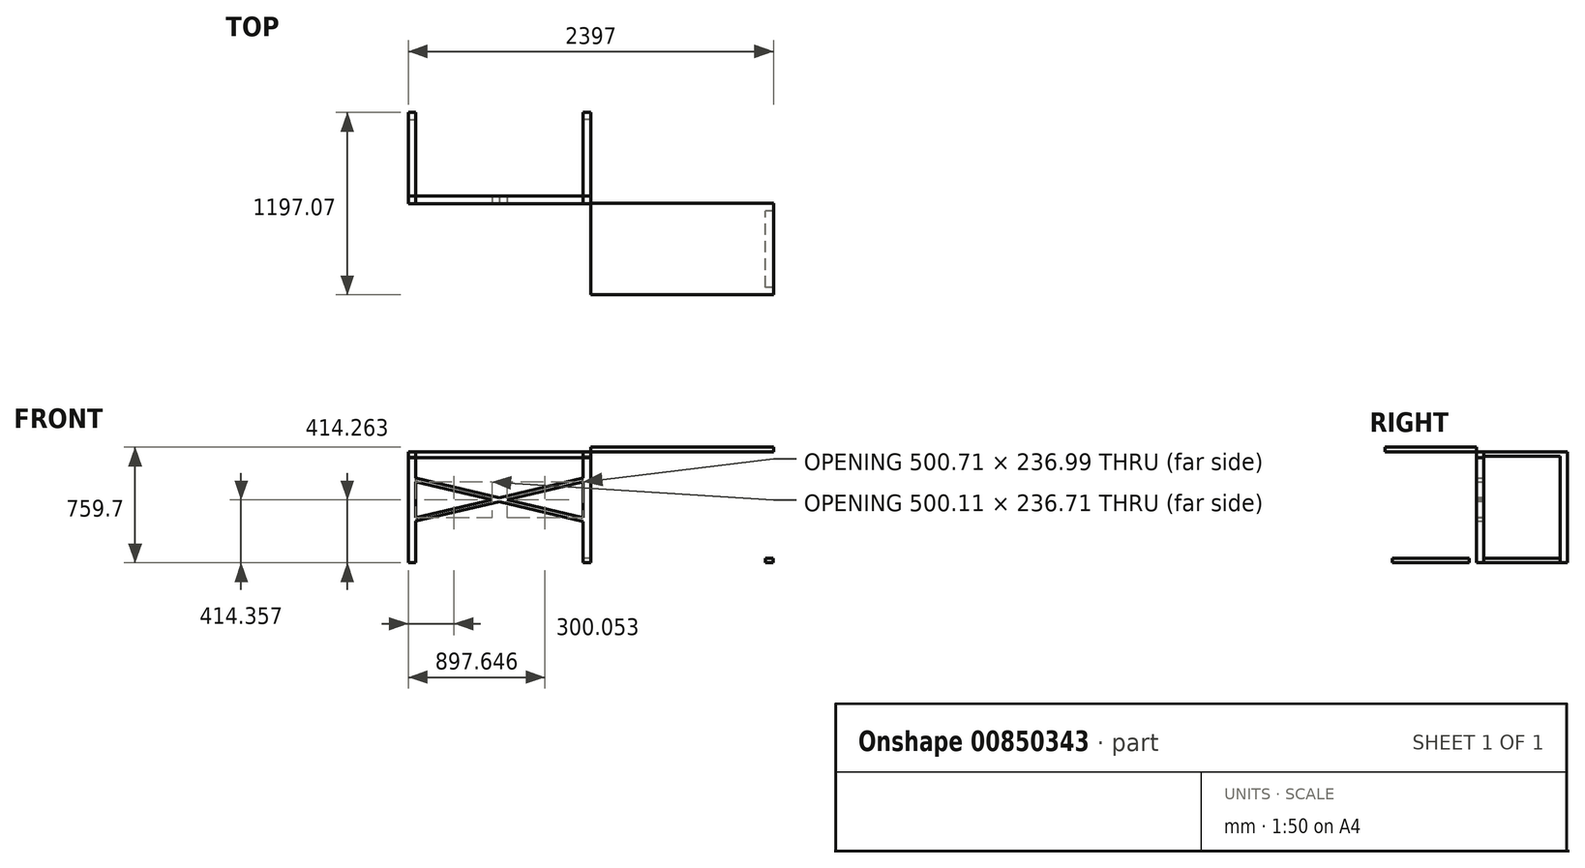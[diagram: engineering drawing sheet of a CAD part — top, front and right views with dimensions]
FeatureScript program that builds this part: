
annotation { "Feature Type Name" : "Feature", "Feature Type Description" : "" }
export const myFeature = defineFeature(function(context is Context, id is Id, definition is map)
    precondition{}
    {
        {
            var Q0;
            Q0=qCreatedBy(makeId("Top.planeOp"),FACE);
            var sketch = newSketch(context, id + "F0", { "sketchPlane" : qUnion([Q0])});
            skLineSegment(sketch, "E0.bottom", {"start": v(600, -300) * mm, "end": v(-600, -300) * mm});
            skLineSegment(sketch, "E0.top", {"start": v(600, 300) * mm, "end": v(-600, 300) * mm});
            skLineSegment(sketch, "E0.left", {"start": v(600, -300) * mm, "end": v(600, 300) * mm});
            skLineSegment(sketch, "E0.right", {"start": v(-600, -300) * mm, "end": v(-600, 300) * mm});
            skPoint(sketch, "E0.middle", {"position": v(0, 0) * mm});
            skSolve(sketch);
        }
        {
            var Q0;
            Q0=qSketchRegion(id+"F0",true);
            extrude(context, id + "F1", {"entities" : qUnion([Q0]), "depth" : 30 * mm, "offsetDistance" : 25 * mm});
        }
        {
            var Q0;
            Q0=qCreatedBy(makeId("Right.planeOp"),FACE);
            var sketch = newSketch(context, id + "F2", { "sketchPlane" : qUnion([Q0])});
            skLineSegment(sketch, "E1.bottom", {"start": v(-299.02, 0) * mm, "end": v(299.02, 0) * mm});
            skLineSegment(sketch, "E1.top", {"start": v(-299.02, -29.7) * mm, "end": v(299.02, -29.7) * mm});
            skLineSegment(sketch, "E1.left", {"start": v(-299.02, 0) * mm, "end": v(-299.02, -29.7) * mm});
            skLineSegment(sketch, "E1.right", {"start": v(299.02, 0) * mm, "end": v(299.02, -29.7) * mm});
            skSolve(sketch);
        }
        {
            var Q0;
            Q0=qSketchRegion(id+"F2",true);
            extrude(context, id + "F3", {"entities" : qUnion([Q0]), "depth" : 50 * mm, "offsetDistance" : 25 * mm});
        }
        {
            var Q0;
            Q0=makeQuery(id+"F3.opExtrude","SWEPT_BODY",BODY,{"disambiguationData":[OSD([sQuery(id+"F2.wireOp",EDGE,"E1.bottom"),sQuery(id+"F2.wireOp",EDGE,"E1.top"),sQuery(id+"F2.wireOp",EDGE,"E1.left"),sQuery(id+"F2.wireOp",EDGE,"E1.right")])]});
            transform(context, id + "F4", {"entities" : qUnion([Q0]), "transformType" : TransformType.TRANSLATION_3D, "dx" : 549 * mm, "dy" : 0 * mm, "dz" : 0 * mm, "makeCopy" : false});
        }
        {
            var Q0;
            Q0=makeQuery(id+"F3.opExtrude","SWEPT_BODY",BODY,{"disambiguationData":[OSD([sQuery(id+"F2.wireOp",EDGE,"E1.bottom"),sQuery(id+"F2.wireOp",EDGE,"E1.top"),sQuery(id+"F2.wireOp",EDGE,"E1.left"),sQuery(id+"F2.wireOp",EDGE,"E1.right")])]});
            var Q1;
            Q1=qCreatedBy(makeId("Right.planeOp"),FACE);
            mirror(context, id + "F5", {"entities" : qUnion([Q0]), "mirrorPlane" : qUnion([Q1])});
        }
        {
            var Q0;
            Q0=makeQuery(id+"F5.opPattern","COPY",FACE,{"derivedFrom":makeQuery(id+"F3.opExtrude","SWEPT_FACE",FACE,{"disambiguationData":[OSD([sQuery(id+"F2.wireOp",EDGE,"E1.top")])]}),"instanceName":"1"});
            var sketch = newSketch(context, id + "F6", { "sketchPlane" : qUnion([Q0])});
            skLineSegment(sketch, "E2.bottom", {"start": v(-599, -299.02) * mm, "end": v(-549, -299.02) * mm});
            skLineSegment(sketch, "E2.top", {"start": v(-599, -251.22) * mm, "end": v(-549, -251.22) * mm});
            skLineSegment(sketch, "E2.left", {"start": v(-599, -299.02) * mm, "end": v(-599, -251.22) * mm});
            skLineSegment(sketch, "E2.right", {"start": v(-549, -299.02) * mm, "end": v(-549, -251.22) * mm});
            skSolve(sketch);
        }
        {
            var Q0;
            Q0=qSketchRegion(id+"F6",true);
            extrude(context, id + "F7", {"entities" : qUnion([Q0]), "depth" : 700 * mm, "offsetDistance" : 25 * mm});
        }
        {
            var Q0;
            Q0=makeQuery(id+"F7.opExtrude","SWEPT_BODY",BODY,{"disambiguationData":[OSD([sQuery(id+"F6.wireOp",EDGE,"E2.bottom"),sQuery(id+"F6.wireOp",EDGE,"E2.top"),sQuery(id+"F6.wireOp",EDGE,"E2.left"),sQuery(id+"F6.wireOp",EDGE,"E2.right")])]});
            var Q1;
            Q1=qCreatedBy(makeId("Right.planeOp"),FACE);
            mirror(context, id + "F8", {"entities" : qUnion([Q0]), "mirrorPlane" : qUnion([Q1])});
        }
        {
            var Q0;
            Q0=makeQuery(id+"F7.opExtrude","SWEPT_BODY",BODY,{"disambiguationData":[OSD([sQuery(id+"F6.wireOp",EDGE,"E2.bottom"),sQuery(id+"F6.wireOp",EDGE,"E2.top"),sQuery(id+"F6.wireOp",EDGE,"E2.left"),sQuery(id+"F6.wireOp",EDGE,"E2.right")])]});
            var Q1;
            Q1=qCreatedBy(makeId("Front.planeOp"),FACE);
            mirror(context, id + "F9", {"operationType" : NewBodyOperationType.ADD, "entities" : qUnion([Q0]), "mirrorPlane" : qUnion([Q1])});
        }
        {
            var Q0;
            Q0=makeQuery(id+"F8.opPattern","COPY",BODY,{"derivedFrom":makeQuery(id+"F7.opExtrude","SWEPT_BODY",BODY,{"disambiguationData":[OSD([sQuery(id+"F6.wireOp",EDGE,"E2.bottom"),sQuery(id+"F6.wireOp",EDGE,"E2.top"),sQuery(id+"F6.wireOp",EDGE,"E2.left"),sQuery(id+"F6.wireOp",EDGE,"E2.right")])]}),"instanceName":"1"});
            var Q1;
            Q1=qCreatedBy(makeId("Front.planeOp"),FACE);
            mirror(context, id + "F10", {"operationType" : NewBodyOperationType.ADD, "entities" : qUnion([Q0]), "mirrorPlane" : qUnion([Q1])});
        }
        {
            var Q0;
            Q0=qCreatedBy(makeId("Top.planeOp"),FACE);
            var sketch = newSketch(context, id + "F11", { "sketchPlane" : qUnion([Q0])});
            skLineSegment(sketch, "E3.bottom", {"start": v(-598.92, -299.03) * mm, "end": v(598.98, -299.03) * mm});
            skLineSegment(sketch, "E3.top", {"start": v(-598.92, -251.27) * mm, "end": v(598.98, -251.27) * mm});
            skLineSegment(sketch, "E3.left", {"start": v(-598.92, -299.03) * mm, "end": v(-598.92, -251.27) * mm});
            skLineSegment(sketch, "E3.right", {"start": v(598.98, -299.03) * mm, "end": v(598.98, -251.27) * mm});
            skSolve(sketch);
        }
        {
            var Q0;
            Q0=qSketchRegion(id+"F11",true);
            extrude(context, id + "F12", {"entities" : qUnion([Q0]), "oppositeDirection" : true, "depth" : 40 * mm, "offsetDistance" : 25 * mm});
        }
        {
            var Q0;
            Q0=makeQuery(id+"F9.opPattern","COPY",FACE,{"derivedFrom":makeQuery(id+"F7.opExtrude","SWEPT_FACE",FACE,{"disambiguationData":[OSD([sQuery(id+"F6.wireOp",EDGE,"E2.top")])]}),"instanceName":"1"});
            var sketch = newSketch(context, id + "F13", { "sketchPlane" : qUnion([Q0])});
            skLineSegment(sketch, "E4.bottom", {"start": v(599, -729.7) * mm, "end": v(549, -729.7) * mm});
            skLineSegment(sketch, "E4.top", {"start": v(599, -699.7) * mm, "end": v(549, -699.7) * mm});
            skLineSegment(sketch, "E4.left", {"start": v(599, -729.7) * mm, "end": v(599, -699.7) * mm});
            skLineSegment(sketch, "E4.right", {"start": v(549, -729.7) * mm, "end": v(549, -699.7) * mm});
            skLineSegment(sketch, "E5.MirrorCS", {"start": v(-599, -729.7) * mm, "end": v(-599, -699.7) * mm});
            skLineSegment(sketch, "E6.MirrorCS", {"start": v(-599, -729.7) * mm, "end": v(-549, -729.7) * mm});
            skLineSegment(sketch, "E7.MirrorCS", {"start": v(-599, -699.7) * mm, "end": v(-549, -699.7) * mm});
            skLineSegment(sketch, "E8.MirrorCS", {"start": v(-549, -729.7) * mm, "end": v(-549, -699.7) * mm});
            skSolve(sketch);
        }
        {
            var Q0;
            Q0=qSketchRegion(id+"F13",true);
            extrude(context, id + "F14", {"entities" : qUnion([Q0]), "depth" : 502.5 * mm, "offsetDistance" : 25 * mm});
        }
        {
            var Q0;
            {var subQ0=makeQuery(id+"F7.opExtrude","SWEPT_FACE",FACE,{"disambiguationData":[OSD([sQuery(id+"F6.wireOp",EDGE,"E2.right")])]});Q0=makeQuery(id+"F9.boolean.opBoolean","MERGE",FACE,{"derivedFrom":[makeQuery(id+"F5.opPattern","COPY",FACE,{"derivedFrom":makeQuery(id+"F3.opExtrude","CAP_FACE",FACE,{"disambiguationData":[OSD([sQuery(id+"F2.wireOp",EDGE,"E1.bottom"),sQuery(id+"F2.wireOp",EDGE,"E1.top"),sQuery(id+"F2.wireOp",EDGE,"E1.left"),sQuery(id+"F2.wireOp",EDGE,"E1.right")])],"isStart":true}),"instanceName":"1"}),subQ0,makeQuery(id+"F9.opPattern","COPY",FACE,{"derivedFrom":subQ0,"instanceName":"1"})]});}
            var sketch = newSketch(context, id + "F15", { "sketchPlane" : qUnion([Q0])});
            skLineSegment(sketch, "E9.bottom", {"start": v(-299.02, -174.08) * mm, "end": v(-251.22, -174.08) * mm});
            skLineSegment(sketch, "E9.top", {"start": v(-299.02, -197.08) * mm, "end": v(-251.22, -197.08) * mm});
            skLineSegment(sketch, "E9.left", {"start": v(-299.02, -174.08) * mm, "end": v(-299.02, -197.08) * mm});
            skLineSegment(sketch, "E9.right", {"start": v(-251.22, -174.08) * mm, "end": v(-251.22, -197.08) * mm});
            skSolve(sketch);
        }
        {
            var Q0;
            {var subQ0=makeQuery(id+"F8.opPattern","COPY",FACE,{"derivedFrom":makeQuery(id+"F7.opExtrude","SWEPT_FACE",FACE,{"disambiguationData":[OSD([sQuery(id+"F6.wireOp",EDGE,"E2.right")])]}),"instanceName":"1"});Q0=makeQuery(id+"F10.boolean.opBoolean","MERGE",FACE,{"derivedFrom":[makeQuery(id+"F3.opExtrude","CAP_FACE",FACE,{"disambiguationData":[OSD([sQuery(id+"F2.wireOp",EDGE,"E1.bottom"),sQuery(id+"F2.wireOp",EDGE,"E1.top"),sQuery(id+"F2.wireOp",EDGE,"E1.left"),sQuery(id+"F2.wireOp",EDGE,"E1.right")])],"isStart":true}),subQ0,makeQuery(id+"F10.opPattern","COPY",FACE,{"derivedFrom":subQ0,"instanceName":"1"})]});}
            var sketch = newSketch(context, id + "F16", { "sketchPlane" : qUnion([Q0])});
            skLineSegment(sketch, "E10.bottom", {"start": v(251.22, -433.84) * mm, "end": v(299.02, -433.84) * mm});
            skLineSegment(sketch, "E10.top", {"start": v(251.22, -456.84) * mm, "end": v(299.02, -456.84) * mm});
            skLineSegment(sketch, "E10.left", {"start": v(251.22, -433.84) * mm, "end": v(251.22, -456.84) * mm});
            skLineSegment(sketch, "E10.right", {"start": v(299.02, -433.84) * mm, "end": v(299.02, -456.84) * mm});
            skSolve(sketch);
        }
        {
            var Q2;
            Q2=makeQuery(id+"F15.imprint","IMPRINT",FACE,{"disambiguationData":[TD([[makeQuery(id+"F15.imprint","IMPRINT",EDGE,{"derivedFrom":sQuery(id+"F15.wireOp",EDGE,"E9.bottom")}),-1.0]])]});
            var Q3;
            Q3=makeQuery(id+"F16.imprint","IMPRINT",FACE,{"disambiguationData":[TD([[makeQuery(id+"F16.imprint","IMPRINT",EDGE,{"derivedFrom":sQuery(id+"F16.wireOp",EDGE,"E10.bottom")}),-1.0]])]});
            loft(context, id + "F17", {"operationType" : NewBodyOperationType.ADD, "sheetProfilesArray" : [{ "sheetProfileEntities" : qUnion([Q2]) }, { "sheetProfileEntities" : qUnion([Q3]) }]});
        }
        {
            var Q0;
            {var subQ0=sQuery(id+"F6.wireOp",EDGE,"E2.top");var subQ9=sQuery(id+"F6.wireOp",EDGE,"E2.right");var subQ10=sQuery(id+"F2.wireOp",EDGE,"E1.top");var subQ12=sQuery(id+"F6.wireOp",EDGE,"E2.bottom");var subQ17=sQuery(id+"F2.wireOp",EDGE,"E1.left");var subQ22=makeQuery(id+"F8.opPattern","COPY",FACE,{"derivedFrom":makeQuery(id+"F7.opExtrude","CAP_FACE",FACE,{"disambiguationData":[OSD([subQ12,subQ0,sQuery(id+"F6.wireOp",EDGE,"E2.left"),subQ9])],"isStart":false}),"instanceName":"1"});var subQ26=makeQuery(id+"F8.opPattern","COPY",FACE,{"derivedFrom":makeQuery(id+"F7.opExtrude","SWEPT_FACE",FACE,{"disambiguationData":[OSD([subQ9])]}),"instanceName":"1"});var subQ27=sQuery(id+"F2.wireOp",EDGE,"E1.right");var subQ28=sQuery(id+"F2.wireOp",EDGE,"E1.bottom");var subQ29=makeQuery(id+"F10.boolean.opBoolean","MERGE",FACE,{"derivedFrom":[makeQuery(id+"F3.opExtrude","CAP_FACE",FACE,{"disambiguationData":[OSD([subQ28,subQ10,subQ17,subQ27])],"isStart":true}),subQ26,makeQuery(id+"F10.opPattern","COPY",FACE,{"derivedFrom":subQ26,"instanceName":"1"})]});Q0=makeQuery(id+"FEgc4e0kRUvku2v_5.opBoolean","MERGE",FACE,{"derivedFrom":[makeQuery(id+"F14.opExtrude","SWEPT_FACE",FACE,{"disambiguationData":[OSD([sQuery(id+"F13.wireOp",EDGE,"E8.MirrorCS")])]}),makeQuery(id+"F17.boolean.opBoolean","SPLIT",FACE,{"disambiguationData":[TD([makeQuery(id+"F3.opExtrude","SWEPT_FACE",FACE,{"disambiguationData":[OSD([subQ28])]})])],"derivedFrom":subQ29}),makeQuery(id+"F17.boolean.opBoolean","SPLIT",FACE,{"disambiguationData":[TD([makeQuery(id+"F10.opPattern","COPY",FACE,{"derivedFrom":subQ22,"instanceName":"1"})])],"derivedFrom":subQ29})]});}
            var sketch = newSketch(context, id + "F18", { "sketchPlane" : qUnion([Q0])});
            skLineSegment(sketch, "E11.bottom", {"start": v(299.02, -173.85) * mm, "end": v(251.22, -173.85) * mm});
            skLineSegment(sketch, "E11.top", {"start": v(299.02, -196.85) * mm, "end": v(251.22, -196.85) * mm});
            skLineSegment(sketch, "E11.left", {"start": v(299.02, -173.85) * mm, "end": v(299.02, -196.85) * mm});
            skLineSegment(sketch, "E11.right", {"start": v(251.22, -173.85) * mm, "end": v(251.22, -196.85) * mm});
            skSolve(sketch);
        }
        {
            var Q0;
            {var subQ0=sQuery(id+"F6.wireOp",EDGE,"E2.bottom");var subQ3=sQuery(id+"F6.wireOp",EDGE,"E2.top");var subQ6=sQuery(id+"F2.wireOp",EDGE,"E1.left");var subQ9=sQuery(id+"F6.wireOp",EDGE,"E2.right");var subQ10=makeQuery(id+"F7.opExtrude","CAP_FACE",FACE,{"disambiguationData":[OSD([subQ0,subQ3,sQuery(id+"F6.wireOp",EDGE,"E2.left"),subQ9])],"isStart":false});var subQ21=sQuery(id+"F2.wireOp",EDGE,"E1.top");var subQ24=makeQuery(id+"F7.opExtrude","SWEPT_FACE",FACE,{"disambiguationData":[OSD([subQ9])]});var subQ25=sQuery(id+"F2.wireOp",EDGE,"E1.right");var subQ26=sQuery(id+"F2.wireOp",EDGE,"E1.bottom");var subQ27=makeQuery(id+"F9.boolean.opBoolean","MERGE",FACE,{"derivedFrom":[makeQuery(id+"F5.opPattern","COPY",FACE,{"derivedFrom":makeQuery(id+"F3.opExtrude","CAP_FACE",FACE,{"disambiguationData":[OSD([subQ26,subQ21,subQ6,subQ25])],"isStart":true}),"instanceName":"1"}),subQ24,makeQuery(id+"F9.opPattern","COPY",FACE,{"derivedFrom":subQ24,"instanceName":"1"})]});Q0=makeQuery(id+"FEgc4e0kRUvku2v_5.opBoolean","MERGE",FACE,{"derivedFrom":[makeQuery(id+"F14.opExtrude","SWEPT_FACE",FACE,{"disambiguationData":[OSD([sQuery(id+"F13.wireOp",EDGE,"E4.right")])]}),makeQuery(id+"F17.boolean.opBoolean","SPLIT",FACE,{"disambiguationData":[TD([makeQuery(id+"F5.opPattern","COPY",FACE,{"derivedFrom":makeQuery(id+"F3.opExtrude","SWEPT_FACE",FACE,{"disambiguationData":[OSD([subQ26])]}),"instanceName":"1"})])],"derivedFrom":subQ27}),makeQuery(id+"F17.boolean.opBoolean","SPLIT",FACE,{"disambiguationData":[TD([makeQuery(id+"F9.opPattern","COPY",FACE,{"derivedFrom":subQ10,"instanceName":"1"})])],"derivedFrom":subQ27})]});}
            var sketch = newSketch(context, id + "F19", { "sketchPlane" : qUnion([Q0])});
            skLineSegment(sketch, "E12.bottom", {"start": v(-299.02, -433.8) * mm, "end": v(-251.22, -433.8) * mm});
            skLineSegment(sketch, "E12.top", {"start": v(-299.02, -456.8) * mm, "end": v(-251.22, -456.8) * mm});
            skLineSegment(sketch, "E12.left", {"start": v(-299.02, -433.8) * mm, "end": v(-299.02, -456.8) * mm});
            skLineSegment(sketch, "E12.right", {"start": v(-251.22, -433.8) * mm, "end": v(-251.22, -456.8) * mm});
            skSolve(sketch);
        }
        {
            var Q1;
            Q1=makeQuery(id+"F19.imprint","IMPRINT",FACE,{"disambiguationData":[TD([[makeQuery(id+"F19.imprint","IMPRINT",EDGE,{"derivedFrom":sQuery(id+"F19.wireOp",EDGE,"E12.bottom")}),-1.0]])]});
            var Q2;
            Q2=makeQuery(id+"F18.imprint","IMPRINT",FACE,{"disambiguationData":[TD([[makeQuery(id+"F18.imprint","IMPRINT",EDGE,{"derivedFrom":sQuery(id+"F18.wireOp",EDGE,"E11.bottom")}),1.0]])]});
            loft(context, id + "F20", {"operationType" : NewBodyOperationType.ADD, "sheetProfilesArray" : [{ "sheetProfileEntities" : qUnion([Q1]) }, { "sheetProfileEntities" : qUnion([Q2]) }]});
        }
        {
            var Q0;
            Q0=makeQuery(id+"F14.opExtrude","SWEPT_BODY",BODY,{"disambiguationData":[OSD([sQuery(id+"F13.wireOp",EDGE,"E4.bottom"),sQuery(id+"F13.wireOp",EDGE,"E4.top"),sQuery(id+"F13.wireOp",EDGE,"E4.left"),sQuery(id+"F13.wireOp",EDGE,"E4.right")])]});
            var Q1;
            Q1=makeQuery(id+"F1.opExtrude","SWEPT_BODY",BODY,{"disambiguationData":[OSD([sQuery(id+"F0.wireOp",EDGE,"E0.bottom"),sQuery(id+"F0.wireOp",EDGE,"E0.top"),sQuery(id+"F0.wireOp",EDGE,"E0.left"),sQuery(id+"F0.wireOp",EDGE,"E0.right")])]});
            var Q2;
            Q2=makeQuery(id+"F10.boolean.opBoolean","MERGE",EDGE,{"derivedFrom":[makeQuery(id+"F3.opExtrude","CAP_EDGE",EDGE,{"disambiguationData":[OSD([sQuery(id+"F2.wireOp",EDGE,"E1.left")])],"isStart":false}),makeQuery(id+"F10.opPattern","COPY",EDGE,{"derivedFrom":makeQuery(id+"F8.opPattern","COPY",EDGE,{"derivedFrom":makeQuery(id+"F7.opExtrude","SWEPT_EDGE",EDGE,{"disambiguationData":[OSD([sQuery(id+"F6.wireOp",EDGE,"E2.bottom"),sQuery(id+"F6.wireOp",EDGE,"E2.left")])]}),"instanceName":"1"}),"instanceName":"1"})]});
            transform(context, id + "F21", {"entities" : qUnion([Q0, Q1]), "transformType" : TransformType.ROTATION, "transformAxis" : qUnion([Q2]), "angle" : 180 * degree, "makeCopy" : false});
        }
    });
